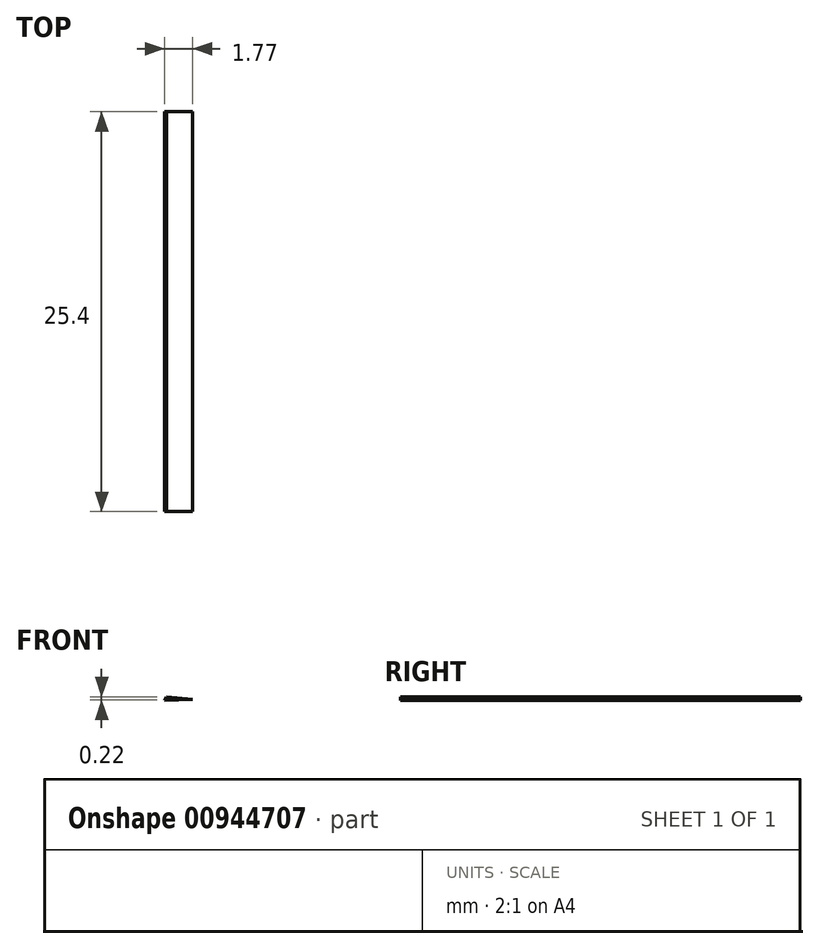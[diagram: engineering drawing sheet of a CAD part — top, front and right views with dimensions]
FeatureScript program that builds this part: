
annotation { "Feature Type Name" : "Feature", "Feature Type Description" : "" }
export const myFeature = defineFeature(function(context is Context, id is Id, definition is map)
    precondition{}
    {
        {
            var Q0;
            Q0=qCreatedBy(makeId("Front.planeOp"),FACE);
            var sketch = newSketch(context, id + "F0", { "sketchPlane" : qUnion([Q0])});
            skLineSegment(sketch, "E0", {"start": v(-691.19, -1377.05) * mm, "end": v(-57.94, -44.5) * mm});
            skLineSegment(sketch, "E1", {"start": v(-1511.68, -74.72) * mm, "end": v(-691.19, -1377.05) * mm});
            skLineSegment(sketch, "E2", {"start": v(16.78, -43.18) * mm, "end": v(-1511.68, -74.72) * mm});
            skLineSegment(sketch, "E3", {"start": v(-56.28, -44.69) * mm, "end": v(-57.94, -44.5) * mm});
            skLineSegment(sketch, "E4", {"start": v(16.78, -43.18) * mm, "end": v(9.92, 1.67) * mm});
            skLineSegment(sketch, "E5", {"start": v(9.92, 1.67) * mm, "end": v(-10.66, 1.67) * mm});
            skLineSegment(sketch, "E6", {"start": v(-10.66, 1.67) * mm, "end": v(-27.74, -44.1) * mm});
            skLineSegment(sketch, "E7.trimOffspring", {"start": v(-27.74, -44.1) * mm, "end": v(-56.28, -44.69) * mm});
            skSolve(sketch);
        }
        {
            var Q0;
            Q0=makeQuery(id+"F0.imprint","IMPRINT",FACE,{"disambiguationData":[TD([[makeQuery(id+"F0.imprint","IMPRINT",EDGE,{"derivedFrom":sQuery(id+"F0.wireOp",EDGE,"E0")}),-1.0]])]});
            extrude(context, id + "F1", {"entities" : qUnion([Q0]), "depth" : 25.4 * mm, "offsetDistance" : 25.4 * mm});
        }
    });
